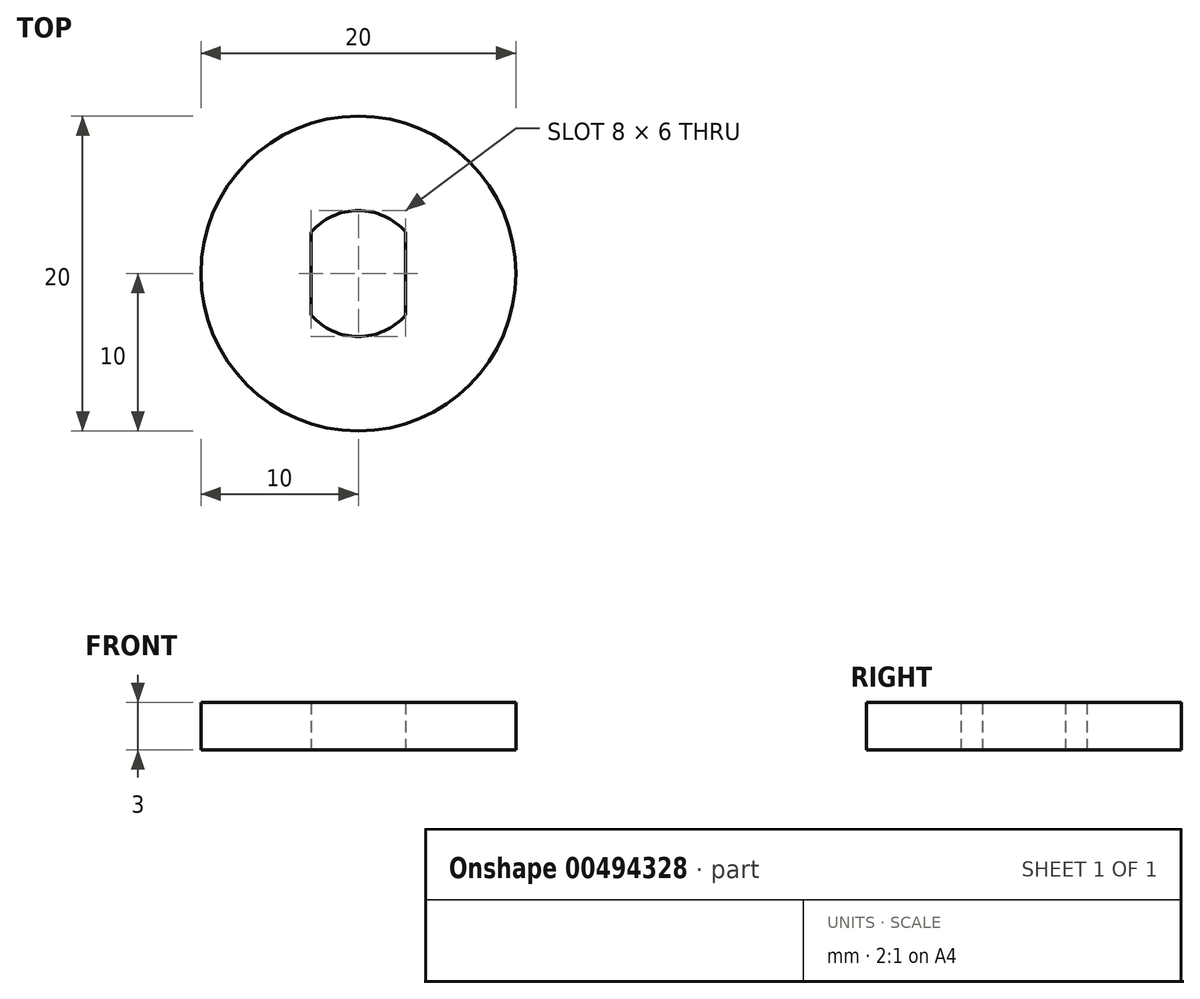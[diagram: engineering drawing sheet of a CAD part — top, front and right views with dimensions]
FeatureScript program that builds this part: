
annotation { "Feature Type Name" : "Feature", "Feature Type Description" : "" }
export const myFeature = defineFeature(function(context is Context, id is Id, definition is map)
    precondition{}
    {
        {
            var Q0;
            Q0=qCreatedBy(makeId("Top.planeOp"),FACE);
            var sketch = newSketch(context, id + "F0", { "sketchPlane" : qUnion([Q0])});
            skCircle(sketch, "E0", {"center": v(0, 0) * mm, "radius": 10 * mm});
            skArc(sketch, "E1", {"start": v(3, 2.65) * mm, "mid": v(0, 4) * mm, "end": v(-3, 2.65) * mm});
            skLineSegment(sketch, "E2.left", {"start": v(-3, 2.65) * mm, "end": v(-3, -2.65) * mm});
            skLineSegment(sketch, "E2.right", {"start": v(3, 2.65) * mm, "end": v(3, -2.65) * mm});
            skArc(sketch, "E3.trimOffspring", {"start": v(-3, -2.65) * mm, "mid": v(0, -4) * mm, "end": v(3, -2.65) * mm});
            skSolve(sketch);
        }
        {
            var Q0;
            Q0=makeQuery(id+"F0.imprint","IMPRINT",FACE,{"disambiguationData":[TD([[makeQuery(id+"F0.imprint","IMPRINT",EDGE,{"derivedFrom":sQuery(id+"F0.wireOp",EDGE,"E0")}),1.0]])]});
            extrude(context, id + "F1", {"entities" : qUnion([Q0]), "depth" : 3 * mm});
        }
    });
